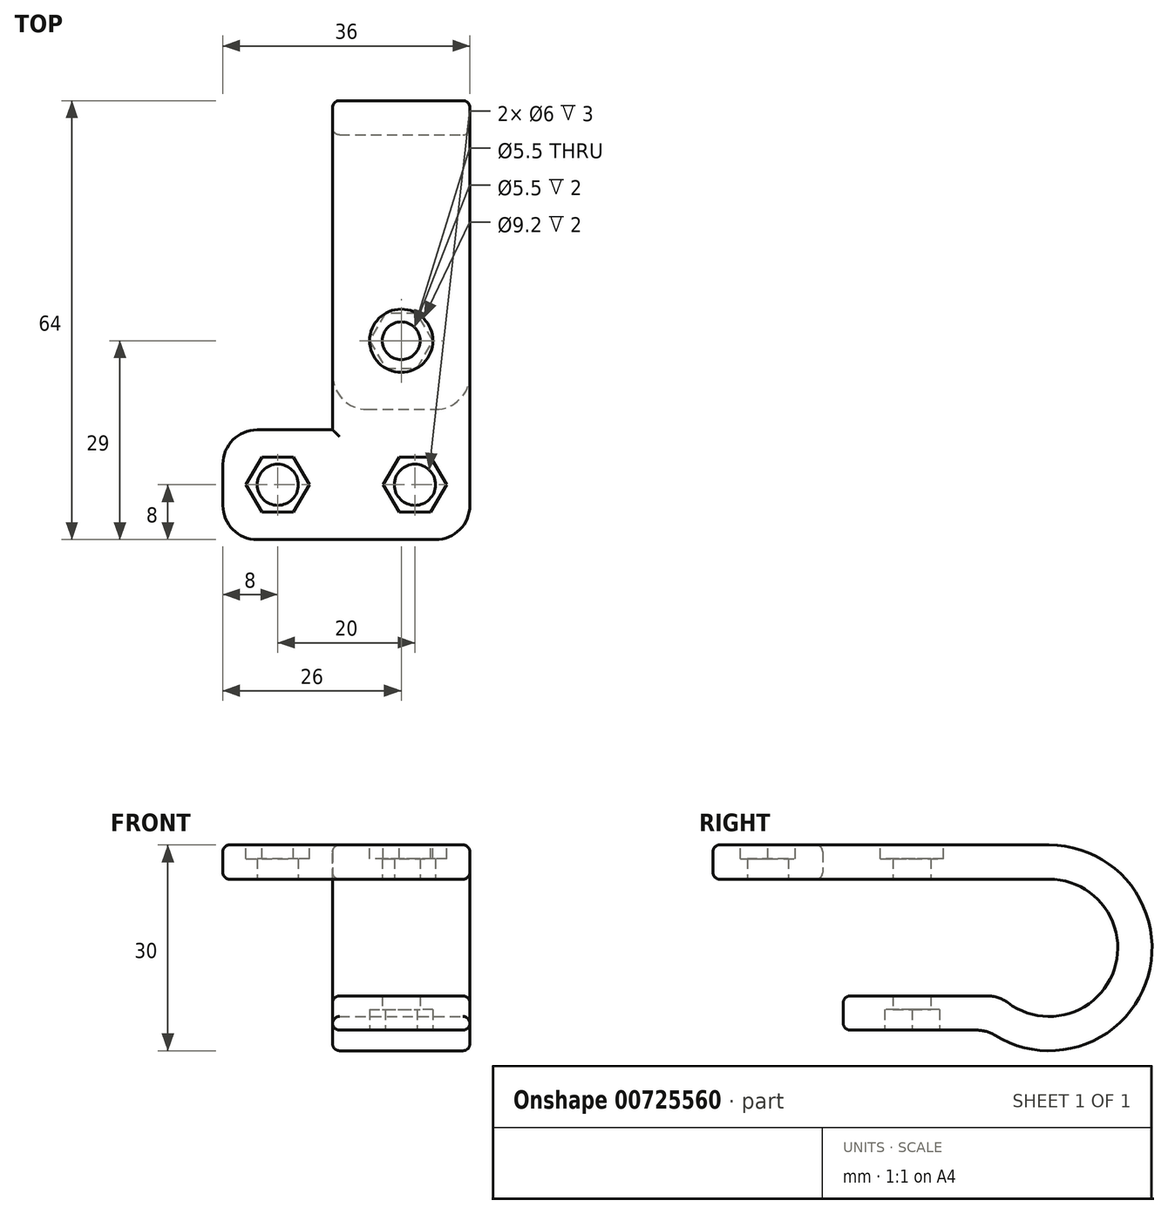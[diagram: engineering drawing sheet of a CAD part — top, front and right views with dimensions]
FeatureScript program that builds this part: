
annotation { "Feature Type Name" : "Feature", "Feature Type Description" : "" }
export const myFeature = defineFeature(function(context is Context, id is Id, definition is map)
    precondition{}
    {
        {
            var Q0;
            Q0=qCreatedBy(makeId("Top.planeOp"),FACE);
            var sketch = newSketch(context, id + "F0", { "sketchPlane" : qUnion([Q0])});
            skCircle(sketch, "E0", {"center": v(-10, 0) * mm, "radius": 3 * mm});
            skCircle(sketch, "E1", {"center": v(10, 0) * mm, "radius": 3 * mm});
            skLineSegment(sketch, "E2", {"start": v(-18, -8) * mm, "end": v(18, -8) * mm});
            skLineSegment(sketch, "E3", {"start": v(-18, 8) * mm, "end": v(18, 8) * mm});
            skPoint(sketch, "E4", {"position": v(13, 0) * mm});
            skLineSegment(sketch, "E5", {"start": v(18, -8) * mm, "end": v(18, 8) * mm});
            skLineSegment(sketch, "E6", {"start": v(-18, 8) * mm, "end": v(-18, -8) * mm});
            skSolve(sketch);
        }
        {
            var Q0;
            Q0=makeQuery(id+"F0.imprint","IMPRINT",FACE,{"disambiguationData":[TD([[makeQuery(id+"F0.imprint","IMPRINT",EDGE,{"derivedFrom":sQuery(id+"F0.wireOp",EDGE,"E0")}),-1.0]])]});
            extrude(context, id + "F1", {"entities" : qUnion([Q0]), "depth" : 5 * mm, "offsetDistance" : 25 * mm});
        }
        {
            var Q0;
            Q0=makeQuery(id+"F1.opExtrude","CAP_FACE",FACE,{"disambiguationData":[OSD([sQuery(id+"F0.wireOp",EDGE,"E0"),sQuery(id+"F0.wireOp",EDGE,"E1"),sQuery(id+"F0.wireOp",EDGE,"E2"),sQuery(id+"F0.wireOp",EDGE,"E3"),sQuery(id+"F0.wireOp",EDGE,"HTNePvBA-ANqU-kaGE-syDm-vdjPT7CEC880"),sQuery(id+"F0.wireOp",EDGE,"CoFUtXaO-UC8f-Wp8c-KHg8-5r4Yufck5tJn")])],"isStart":false});
            var sketch = newSketch(context, id + "F2", { "sketchPlane" : qUnion([Q0])});
            skCircle(sketch, "E7.cCircle", {"center": v(-10, 0) * mm, "radius": 4 * mm, "construction": true});
            skLineSegment(sketch, "E7.0", {"start": v(-12.3, 4) * mm, "end": v(-7.7, 4) * mm});
            skLineSegment(sketch, "E7.1", {"start": v(-7.7, 4) * mm, "end": v(-5.38, 0) * mm});
            skLineSegment(sketch, "E7.2", {"start": v(-5.38, 0) * mm, "end": v(-7.7, -4) * mm});
            skLineSegment(sketch, "E7.3", {"start": v(-7.7, -4) * mm, "end": v(-12.3, -4) * mm});
            skLineSegment(sketch, "E7.4", {"start": v(-12.3, -4) * mm, "end": v(-14.62, 0) * mm});
            skLineSegment(sketch, "E7.5", {"start": v(-14.62, 0) * mm, "end": v(-12.3, 4) * mm});
            skPoint(sketch, "E7.0.midPoint", {"position": v(-10, 4) * mm});
            skCircle(sketch, "E8.cCircle", {"center": v(10, 0) * mm, "radius": 4 * mm, "construction": true});
            skLineSegment(sketch, "E8.0", {"start": v(7.7, 4) * mm, "end": v(12.3, 4) * mm});
            skLineSegment(sketch, "E8.1", {"start": v(12.3, 4) * mm, "end": v(14.62, 0) * mm});
            skLineSegment(sketch, "E8.2", {"start": v(14.62, 0) * mm, "end": v(12.3, -4) * mm});
            skLineSegment(sketch, "E8.3", {"start": v(12.3, -4) * mm, "end": v(7.7, -4) * mm});
            skLineSegment(sketch, "E8.4", {"start": v(7.7, -4) * mm, "end": v(5.38, 0) * mm});
            skLineSegment(sketch, "E8.5", {"start": v(5.38, 0) * mm, "end": v(7.7, 4) * mm});
            skPoint(sketch, "E8.0.midPoint", {"position": v(10, 4) * mm});
            skSolve(sketch);
        }
        {
            var Q0;
            Q0=makeQuery(id+"F2.imprint","IMPRINT",FACE,{"disambiguationData":[TD([[makeQuery(id+"F2.imprint","IMPRINT",EDGE,{"derivedFrom":sQuery(id+"F2.wireOp",EDGE,"E8.0")}),-1.0]])]});
            var Q1;
            Q1=makeQuery(id+"F2.imprint","IMPRINT",FACE,{"disambiguationData":[TD([[makeQuery(id+"F2.imprint","IMPRINT",EDGE,{"derivedFrom":sQuery(id+"F2.wireOp",EDGE,"E7.0")}),-1.0]])]});
            extrude(context, id + "F3", {"entities" : qUnion([Q0, Q1]), "operationType" : NewBodyOperationType.REMOVE, "oppositeDirection" : true, "depth" : 2 * mm, "offsetDistance" : 25 * mm});
        }
        {
            var Q0;
            Q0=qCreatedBy(makeId("Right.planeOp"),FACE);
            cPlane(context, id + "F4", {"entities" : qUnion([Q0]), "cplaneType" : CPlaneType.OFFSET, "offset" : 18 * mm, "width" : 150 * mm, "height" : 150 * mm});
        }
        {
            var Q0;
            Q0=qCreatedBy(id+"F4.planeOp",FACE);
            var sketch = newSketch(context, id + "F5", { "sketchPlane" : qUnion([Q0])});
            skCircle(sketch, "E9", {"center": v(41, -10) * mm, "radius": 10 * mm});
            skCircle(sketch, "E10", {"center": v(41, -10) * mm, "radius": 15 * mm});
            skLineSegment(sketch, "E11", {"start": v(8, 0) * mm, "end": v(41, 0) * mm});
            skLineSegment(sketch, "E12", {"start": v(41, 5) * mm, "end": v(8, 5) * mm});
            skLineSegment(sketch, "E13.bottom", {"start": v(33.86, -17) * mm, "end": v(11, -17) * mm});
            skLineSegment(sketch, "E13.top", {"start": v(33.86, -22) * mm, "end": v(11, -22) * mm});
            skLineSegment(sketch, "E13.left", {"start": v(33.86, -17) * mm, "end": v(33.86, -22) * mm});
            skLineSegment(sketch, "E13.right", {"start": v(11, -17) * mm, "end": v(11, -22) * mm});
            skLineSegment(sketch, "E14", {"start": v(8, 5) * mm, "end": v(8, 0) * mm});
            skPoint(sketch, "E15", {"position": v(26, -10) * mm});
            skSolve(sketch);
        }
        {
            var Q0;
            {var subQ8=sQuery(id+"F5.wireOp",EDGE,"E13.left");Q0=makeQuery(id+"F5.imprint","IMPRINT",FACE,{"disambiguationData":[TD([[makeQuery(id+"F5.imprint","IMPRINT",EDGE,{"derivedFrom":subQ8}),1.0]])]});}
            var Q1;
            {var subQ5=sQuery(id+"F5.wireOp",EDGE,"E13.left");Q1=makeQuery(id+"F5.imprint","IMPRINT",FACE,{"disambiguationData":[TD([[makeQuery(id+"F5.imprint","IMPRINT",EDGE,{"derivedFrom":subQ5}),-1.0]])]});}
            var Q2;
            {var subQ5=sQuery(id+"F5.wireOp",EDGE,"E13.right");Q2=makeQuery(id+"F5.imprint","IMPRINT",FACE,{"disambiguationData":[TD([[makeQuery(id+"F5.imprint","IMPRINT",EDGE,{"derivedFrom":subQ5}),1.0]])]});}
            var Q3;
            {var subQ0=sQuery(id+"F5.wireOp",EDGE,"E11");Q3=makeQuery(id+"F5.imprint","IMPRINT",FACE,{"disambiguationData":[TD([[makeQuery(id+"F5.imprint","IMPRINT",EDGE,{"derivedFrom":subQ0}),1.0]])]});}
            extrude(context, id + "F6", {"entities" : qUnion([Q0, Q1, Q2, Q3]), "operationType" : NewBodyOperationType.ADD, "oppositeDirection" : true, "depth" : 20 * mm, "offsetDistance" : 25 * mm});
        }
        {
            var Q0;
            Q0=makeQuery(id+"F6.opExtrude","SWEPT_FACE",FACE,{"disambiguationData":[OSD([sQuery(id+"F5.wireOp",EDGE,"E13.top")])]});
            var sketch = newSketch(context, id + "F7", { "sketchPlane" : qUnion([Q0])});
            skPoint(sketch, "E16", {"position": v(8, -21) * mm});
            skPoint(sketch, "E17", {"position": v(8, -11) * mm});
            skSolve(sketch);
        }
        {
            var Q0;
            Q0=sQuery(id+"F7.wireOp",VERTEX,"E16");
            var Q1;
            Q1=makeQuery(id+"F1.opExtrude","SWEPT_BODY",BODY,{"disambiguationData":[OSD([sQuery(id+"F0.wireOp",EDGE,"E0"),sQuery(id+"F0.wireOp",EDGE,"E1"),sQuery(id+"F0.wireOp",EDGE,"E2"),sQuery(id+"F0.wireOp",EDGE,"E3"),sQuery(id+"F0.wireOp",EDGE,"HTNePvBA-ANqU-kaGE-syDm-vdjPT7CEC880"),sQuery(id+"F0.wireOp",EDGE,"4baf5908-119d-48d5-820d-0a66f10f85ae"),sQuery(id+"F0.wireOp",EDGE,"E5")])]});
            hole(context, id + "F8", {"style" : HoleStyle.SIMPLE, "endStyle" : HoleEndStyle.THROUGH, "standardTappedOrClearance" : lookupTablePath({ "standard" : "ISO", "fit" : "Normal", "size" : "M5", "type" : "Clearance" }), "standardBlindInLast" : lookupTablePath({ "fit" : "Standard", "standard" : "ISO", "size" : "M5", "type" : "Clearance" }), "holeDiameter" : 5.5 * mm, "majorDiameter" : 5 * mm, "isTappedThrough" : true, "tappedDepth" : 8.5 * mm, "tapClearance" : 3, "startFromSketch" : true, "locations" : qUnion([Q0]), "scope" : qUnion([Q1])});
        }
        {
            var Q0;
            Q0=makeQuery(id+"F6.opExtrude","SWEPT_FACE",FACE,{"disambiguationData":[OSD([sQuery(id+"F5.wireOp",EDGE,"E13.top")])]});
            var sketch = newSketch(context, id + "F9", { "sketchPlane" : qUnion([Q0])});
            skCircle(sketch, "E18.cCircle", {"center": v(8, -21) * mm, "radius": 4 * mm, "construction": true});
            skLineSegment(sketch, "E18.0", {"start": v(5.7, -17) * mm, "end": v(10.3, -17) * mm});
            skLineSegment(sketch, "E18.1", {"start": v(10.3, -17) * mm, "end": v(12.62, -21) * mm});
            skLineSegment(sketch, "E18.2", {"start": v(12.62, -21) * mm, "end": v(10.3, -25) * mm});
            skLineSegment(sketch, "E18.3", {"start": v(10.3, -25) * mm, "end": v(5.7, -25) * mm});
            skLineSegment(sketch, "E18.4", {"start": v(5.7, -25) * mm, "end": v(3.38, -21) * mm});
            skLineSegment(sketch, "E18.5", {"start": v(3.38, -21) * mm, "end": v(5.7, -17) * mm});
            skPoint(sketch, "E18.0.midPoint", {"position": v(8, -17) * mm});
            skSolve(sketch);
        }
        {
            var Q0;
            Q0=makeQuery(id+"F9.imprint","IMPRINT",FACE,{"disambiguationData":[TD([[makeQuery(id+"F9.imprint","IMPRINT",EDGE,{"derivedFrom":sQuery(id+"F9.wireOp",EDGE,"E18.0")}),-1.0]])]});
            extrude(context, id + "F10", {"entities" : qUnion([Q0]), "operationType" : NewBodyOperationType.REMOVE, "oppositeDirection" : true, "depth" : 3 * mm, "offsetDistance" : 25 * mm});
        }
        {
            var Q0;
            Q0=makeQuery(id+"F6.boolean.opBoolean","MERGE",FACE,{"derivedFrom":[makeQuery(id+"F1.opExtrude","CAP_FACE",FACE,{"disambiguationData":[OSD([sQuery(id+"F0.wireOp",EDGE,"E0"),sQuery(id+"F0.wireOp",EDGE,"E1"),sQuery(id+"F0.wireOp",EDGE,"E2"),sQuery(id+"F0.wireOp",EDGE,"E3"),sQuery(id+"F0.wireOp",EDGE,"E5"),sQuery(id+"F0.wireOp",EDGE,"E6")])],"isStart":false}),makeQuery(id+"F6.opExtrude","SWEPT_FACE",FACE,{"disambiguationData":[OSD([sQuery(id+"F5.wireOp",EDGE,"E12")])]})]});
            var sketch = newSketch(context, id + "F11", { "sketchPlane" : qUnion([Q0])});
            skCircle(sketch, "E19", {"center": v(8, 21) * mm, "radius": 4.6 * mm});
            skSolve(sketch);
        }
        {
            var Q0;
            Q0=makeQuery(id+"F11.imprint","IMPRINT",FACE,{"disambiguationData":[TD([[makeQuery(id+"F11.imprint","IMPRINT",EDGE,{"derivedFrom":sQuery(id+"F11.wireOp",EDGE,"E19")}),1.0]])]});
            extrude(context, id + "F12", {"entities" : qUnion([Q0]), "operationType" : NewBodyOperationType.REMOVE, "oppositeDirection" : true, "depth" : 2 * mm, "offsetDistance" : 25 * mm});
        }
        {
            var Q0;
            Q0=makeQuery(id+"F6.opExtrude","CAP_EDGE",EDGE,{"disambiguationData":[OSD([sQuery(id+"F5.wireOp",EDGE,"E14")])],"isStart":false});
            var Q1;
            Q1=makeQuery(id+"F1.opExtrude","SWEPT_EDGE",EDGE,{"disambiguationData":[OSD([sQuery(id+"F0.wireOp",EDGE,"E3"),sQuery(id+"F0.wireOp",EDGE,"E6")])]});
            var Q2;
            Q2=makeQuery(id+"F1.opExtrude","SWEPT_EDGE",EDGE,{"disambiguationData":[OSD([sQuery(id+"F0.wireOp",EDGE,"E2"),sQuery(id+"F0.wireOp",EDGE,"E6")])]});
            var Q3;
            Q3=makeQuery(id+"F1.opExtrude","SWEPT_EDGE",EDGE,{"disambiguationData":[OSD([sQuery(id+"F0.wireOp",EDGE,"E2"),sQuery(id+"F0.wireOp",EDGE,"E5")])]});
            var Q4;
            Q4=makeQuery(id+"F6.opExtrude","SWEPT_EDGE",EDGE,{"disambiguationData":[OSD([sQuery(id+"F5.wireOp",EDGE,"E9"),sQuery(id+"F5.wireOp",EDGE,"E13.bottom"),sQuery(id+"F5.wireOp",EDGE,"E13.left")])]});
            var Q5;
            Q5=makeQuery(id+"F6.opExtrude","SWEPT_EDGE",EDGE,{"disambiguationData":[OSD([sQuery(id+"F5.wireOp",EDGE,"E10"),sQuery(id+"F5.wireOp",EDGE,"E13.top")])]});
            var Q6;
            Q6=makeQuery(id+"F6.opExtrude","CAP_EDGE",EDGE,{"disambiguationData":[OSD([sQuery(id+"F5.wireOp",EDGE,"E13.right")])],"isStart":false});
            var Q7;
            Q7=makeQuery(id+"F6.opExtrude","CAP_EDGE",EDGE,{"disambiguationData":[OSD([sQuery(id+"F5.wireOp",EDGE,"E13.right")])],"isStart":true});
            fillet(context, id + "F13", {"entities" : qUnion([Q0, Q1, Q2, Q3, Q4, Q5, Q6, Q7]), "radius" : 5 * mm, "tangentPropagation" : true, "allowEdgeOverflow" : false});
        }
        {
            var Q0;
            Q0=makeQuery(id+"F6.opExtrude","CAP_EDGE",EDGE,{"disambiguationData":[OSD([sQuery(id+"F5.wireOp",EDGE,"E13.bottom")])],"isStart":false});
            var Q1;
            Q1=makeQuery(id+"F6.opExtrude","CAP_EDGE",EDGE,{"disambiguationData":[OSD([sQuery(id+"F5.wireOp",EDGE,"E13.top")])],"isStart":false});
            fillet(context, id + "F14", {"entities" : qUnion([Q0, Q1]), "radius" : 1 * mm, "tangentPropagation" : true, "allowEdgeOverflow" : false});
        }
    });
